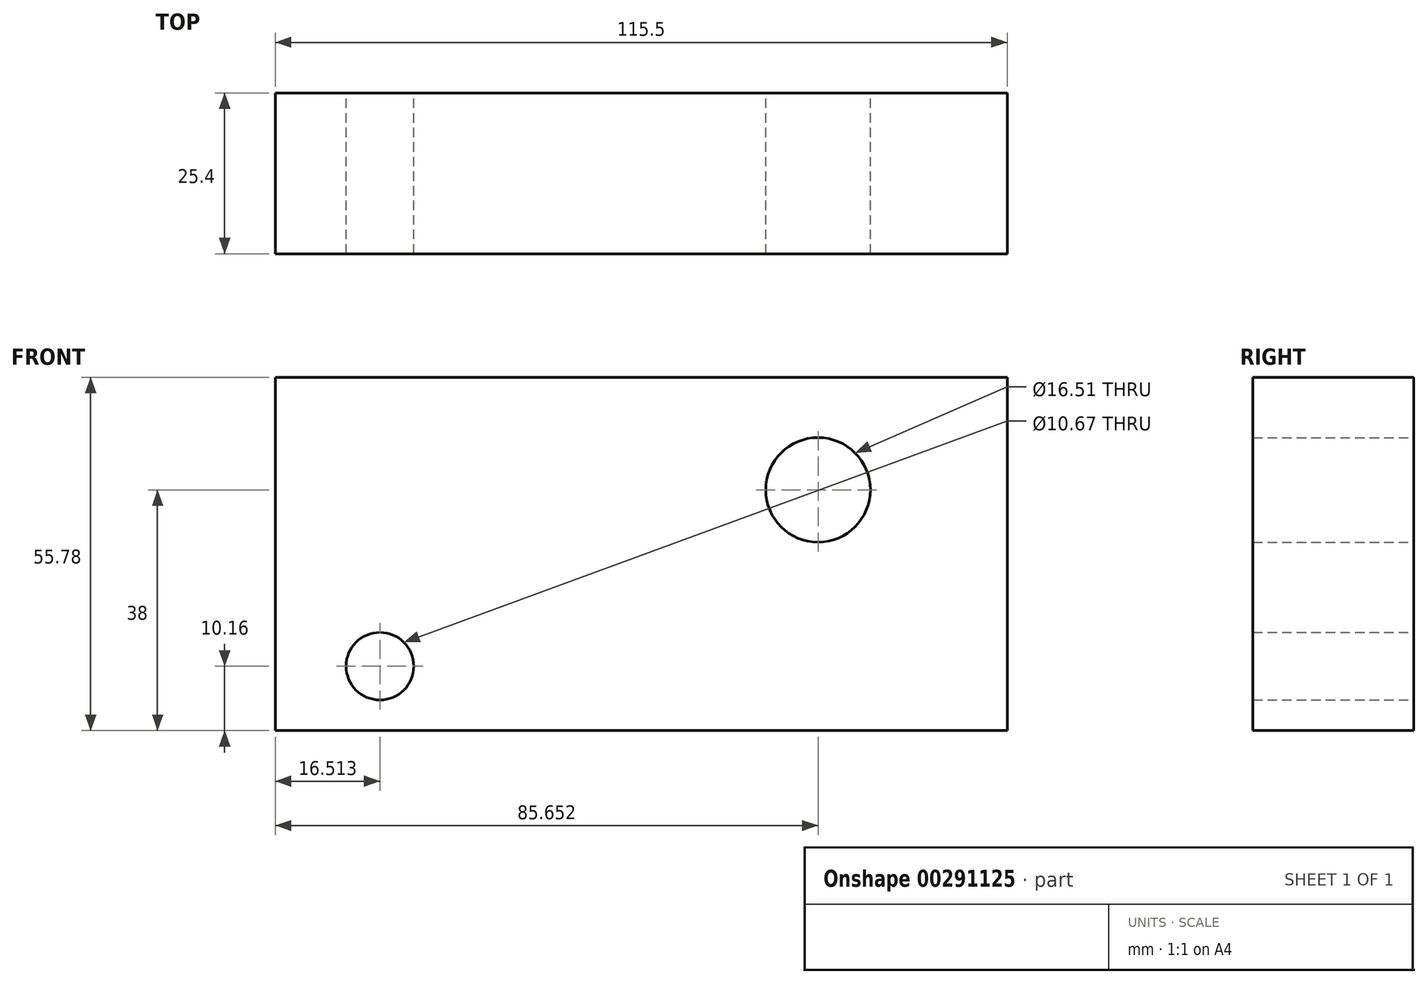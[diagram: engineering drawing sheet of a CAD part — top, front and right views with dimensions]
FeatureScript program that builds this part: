
annotation { "Feature Type Name" : "Feature", "Feature Type Description" : "" }
export const myFeature = defineFeature(function(context is Context, id is Id, definition is map)
    precondition{}
    {
        {
            var Q0;
            Q0=qCreatedBy(makeId("Front.planeOp"),FACE);
            var sketch = newSketch(context, id + "F0", { "sketchPlane" : qUnion([Q0])});
            skLineSegment(sketch, "E0.bottom", {"start": v(57.75, 27.89) * mm, "end": v(-57.75, 27.89) * mm});
            skLineSegment(sketch, "E0.top", {"start": v(57.75, -27.89) * mm, "end": v(-57.75, -27.89) * mm});
            skLineSegment(sketch, "E0.left", {"start": v(57.75, 27.89) * mm, "end": v(57.75, -27.89) * mm});
            skLineSegment(sketch, "E0.right", {"start": v(-57.75, 27.89) * mm, "end": v(-57.75, -27.89) * mm});
            skPoint(sketch, "E0.middle", {"position": v(0, 0) * mm});
            skCircle(sketch, "E1", {"center": v(27.9, 10.1) * mm, "radius": 8.26 * mm});
            skCircle(sketch, "E2", {"center": v(-41.24, -17.73) * mm, "radius": 5.33 * mm});
            skSolve(sketch);
        }
        {
            var Q0;
            Q0=makeQuery(id+"F0.imprint","IMPRINT",FACE,{"disambiguationData":[TD([[makeQuery(id+"F0.imprint","IMPRINT",EDGE,{"derivedFrom":sQuery(id+"F0.wireOp",EDGE,"E0.bottom")}),1.0]])]});
            extrude(context, id + "F1", {"entities" : qUnion([Q0]), "endBound" : BoundingType.SYMMETRIC, "depth" : 25.4 * mm});
        }
    });
